MODEL slx_f1deddcfe8d3
CONFIG AbsTol = auto
CONFIG EnableMultiTasking = on
CONFIG FixedStep = auto
CONFIG MaxStep = auto
CONFIG MinStep = auto
CONFIG RelTol = 1e-3
CONFIG SampleTimeConstraint = Unconstrained
CONFIG SolverName = ode45
CONFIG StartTime = 0.0
CONFIG StopTime = 10.0
BLOCK [SubSystem] Crane
BLOCK [Sum] Crane/Add2
  IconShape = rectangular
  Inputs = +-
BLOCK [Constant] Crane/Constant1
  Value = mPend+mCart
BLOCK [Constant] Crane/Constant3
  Value = mPend*L*L
BLOCK [Product] Crane/Divide
  Inputs = */
BLOCK [Product] Crane/Divide1
  Inputs = */
BLOCK [Inport] Crane/F
  Port = 2
BLOCK [Gain] Crane/Gain
  Gain = mPend*L
BLOCK [Gain] Crane/Gain2
  Gain = mPend*L
BLOCK [Gain] Crane/Gain3
  Gain = mPend*L*g
BLOCK [Integrator] Crane/Integrator
  ContinuousStateAttributes = 'x'
BLOCK [Integrator] Crane/Integrator1
  ContinuousStateAttributes = 'xdot'
BLOCK [Integrator] Crane/Integrator2
  ContinuousStateAttributes = 'theta'
BLOCK [Integrator] Crane/Integrator3
  ContinuousStateAttributes = 'thetadot'
BLOCK [Product] Crane/Product
BLOCK [Product] Crane/Product1
BLOCK [Product] Crane/Product2
BLOCK [Product] Crane/Product3
BLOCK [Trigonometry] Crane/Sin
  Operator = cos
BLOCK [Sum] Crane/Sum
  Inputs = |-++
BLOCK [Sum] Crane/Sum1
  Inputs = |--
BLOCK [Trigonometry] Crane/Trigonometric Function
BLOCK [Inport] Crane/dF
BLOCK [Outport] Crane/theta
  Port = 3
  VectorParamsAs1DForOutWhenUnconnected = off
BLOCK [Outport] Crane/theta_dot
  Port = 4
  VectorParamsAs1DForOutWhenUnconnected = off
BLOCK [Outport] Crane/x
  VectorParamsAs1DForOutWhenUnconnected = off
BLOCK [Outport] Crane/x_dot
  Port = 2
  VectorParamsAs1DForOutWhenUnconnected = off
BLOCK [Inport] F
  Port = 2
BLOCK [Inport] dF
BLOCK [Outport] theta
  Port = 3
  VectorParamsAs1DForOutWhenUnconnected = off
BLOCK [Outport] theta_dot
  Port = 4
  VectorParamsAs1DForOutWhenUnconnected = off
BLOCK [Outport] x
  VectorParamsAs1DForOutWhenUnconnected = off
BLOCK [Outport] x_dot
  Port = 2
  VectorParamsAs1DForOutWhenUnconnected = off
LINE Crane/Add2:1 -> Crane/Sum:2
LINE Crane/Constant1:1 -> Crane/Divide:2
LINE Crane/Constant3:1 -> Crane/Divide1:2
LINE Crane/Divide1:1 -> Crane/Integrator3:1
LINE Crane/Divide1:1 -> Crane/Product:1
LINE Crane/Divide:1 -> Crane/Integrator1:1
LINE Crane/Divide:1 -> Crane/Product3:2
LINE Crane/F:1 -> Crane/Add2:1
LINE Crane/Gain2:1 -> Crane/Sum1:1
LINE Crane/Gain3:1 -> Crane/Sum1:2
LINE Crane/Gain:1 -> Crane/Sum:1
LINE Crane/Integrator1:1 -> Crane/Integrator:1
LINE Crane/Integrator1:1 -> Crane/x_dot:1
LINE Crane/Integrator2:1 -> Crane/Sin:1
LINE Crane/Integrator2:1 -> Crane/Trigonometric Function:1
LINE Crane/Integrator2:1 -> Crane/theta:1
LINE Crane/Integrator3:1 -> Crane/Integrator2:1
LINE Crane/Integrator3:1 -> Crane/Product1:1
LINE Crane/Integrator3:1 -> Crane/Product1:2
LINE Crane/Integrator3:1 -> Crane/theta_dot:1
LINE Crane/Integrator:1 -> Crane/x:1
LINE Crane/Product1:1 -> Crane/Product2:1
LINE Crane/Product2:1 -> Crane/Sum:3
LINE Crane/Product3:1 -> Crane/Gain2:1
LINE Crane/Product:1 -> Crane/Gain:1
LINE Crane/Sin:1 -> Crane/Product3:1
LINE Crane/Sin:1 -> Crane/Product:2
LINE Crane/Sum1:1 -> Crane/Divide1:1
LINE Crane/Sum:1 -> Crane/Divide:1
LINE Crane/Trigonometric Function:1 -> Crane/Gain3:1
LINE Crane/Trigonometric Function:1 -> Crane/Product2:2
LINE Crane/dF:1 -> Crane/Add2:2
LINE Crane:1 -> x:1
LINE Crane:2 -> x_dot:1
LINE Crane:3 -> theta:1
LINE Crane:4 -> theta_dot:1
LINE F:1 -> Crane:2
LINE dF:1 -> Crane:1
